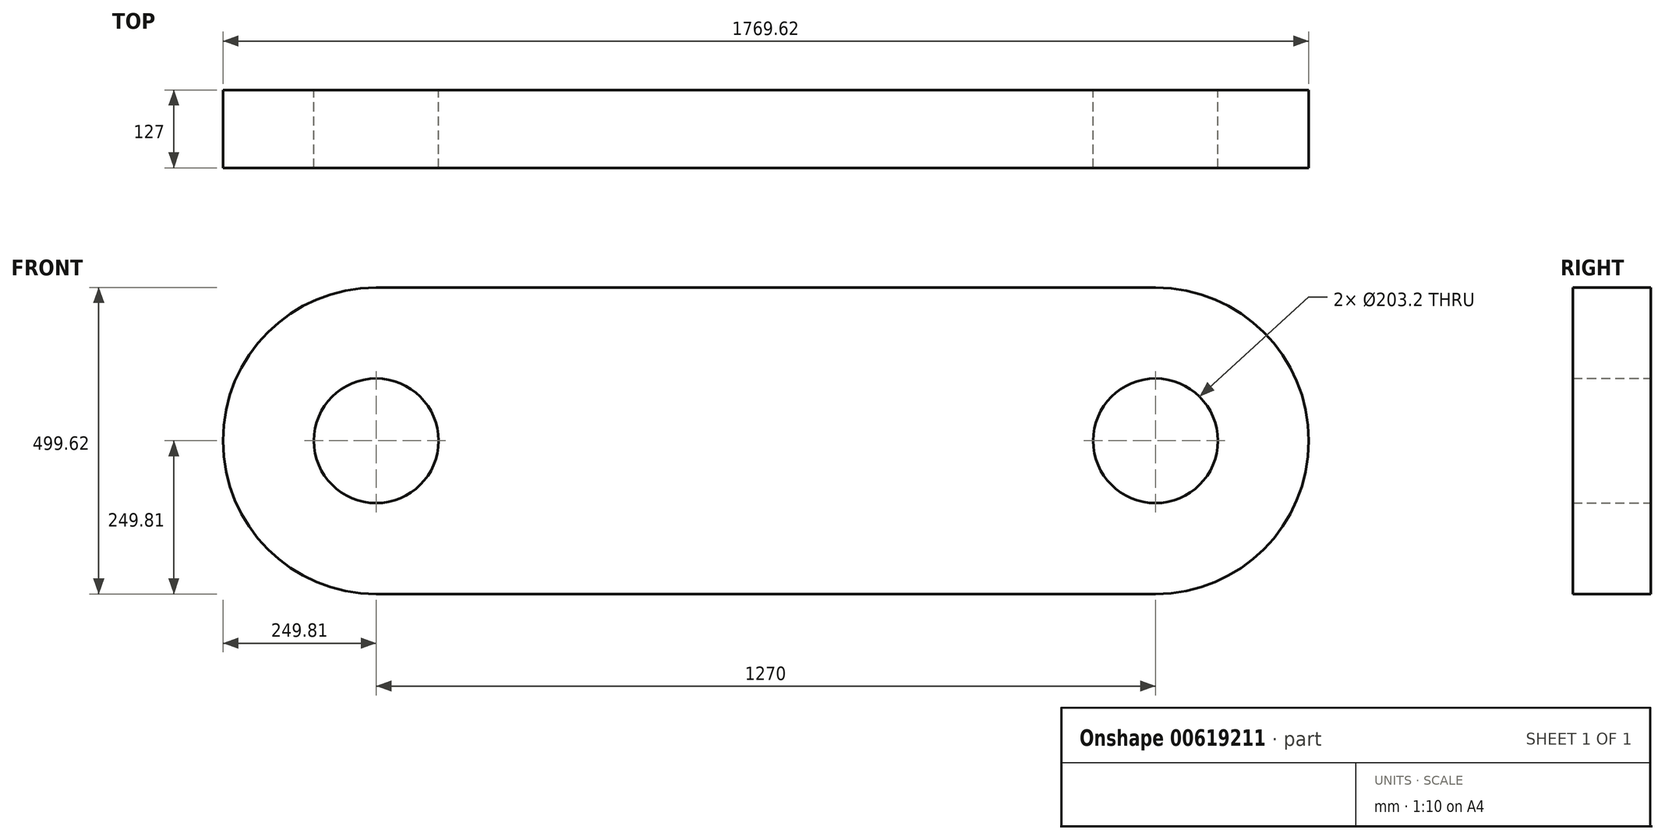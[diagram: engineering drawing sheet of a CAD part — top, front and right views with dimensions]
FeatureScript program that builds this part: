
annotation { "Feature Type Name" : "Feature", "Feature Type Description" : "" }
export const myFeature = defineFeature(function(context is Context, id is Id, definition is map)
    precondition{}
    {
        {
            var Q0;
            Q0=qCreatedBy(makeId("Front.planeOp"),FACE);
            var sketch = newSketch(context, id + "F0", { "sketchPlane" : qUnion([Q0])});
            skArc(sketch, "E0", {"start": v(0, -249.8) * mm, "mid": v(249.8, 0) * mm, "end": v(0, 249.8) * mm});
            skArc(sketch, "E1", {"start": v(-1270, 249.8) * mm, "mid": v(-1519.8, 0) * mm, "end": v(-1270, -249.8) * mm});
            skLineSegment(sketch, "E2", {"start": v(-1270, 249.8) * mm, "end": v(0, 249.8) * mm});
            skLineSegment(sketch, "E3", {"start": v(-1270, -249.8) * mm, "end": v(0, -249.8) * mm});
            skCircle(sketch, "E4", {"center": v(-1270, 0) * mm, "radius": 101.6 * mm});
            skCircle(sketch, "E5", {"center": v(0, 0) * mm, "radius": 101.6 * mm});
            skSolve(sketch);
        }
        {
            var Q0;
            Q0=makeQuery(id+"F0.imprint","IMPRINT",FACE,{"disambiguationData":[TD([[makeQuery(id+"F0.imprint","IMPRINT",EDGE,{"derivedFrom":sQuery(id+"F0.wireOp",EDGE,"E0")}),1.0]])]});
            extrude(context, id + "F1", {"entities" : qUnion([Q0]), "depth" : 127 * mm, "offsetDistance" : 25.4 * mm});
        }
    });
